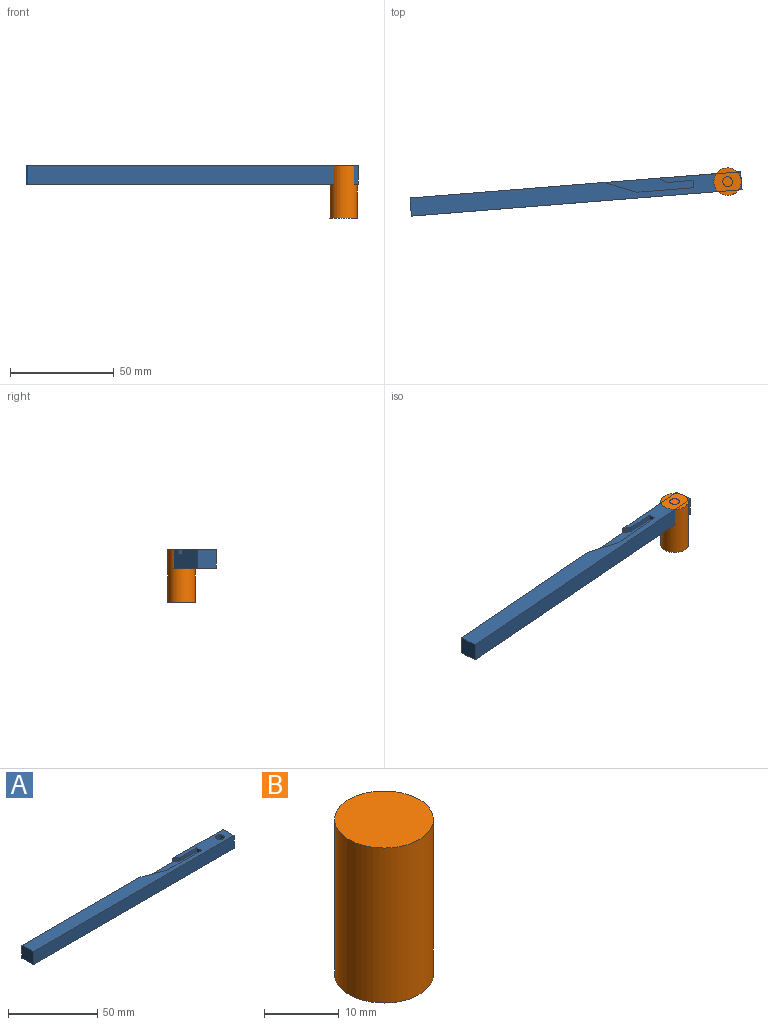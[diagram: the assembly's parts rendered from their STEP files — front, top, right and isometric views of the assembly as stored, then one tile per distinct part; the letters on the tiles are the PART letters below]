
ASSEMBLY  parts=2 mates=1
PART A: 15 faces, bbox 159.6x8.7x8.9 mm
  f0: plane 39.88x0.13mm, normal (0,0,1), area 2.6mm2, adj f3,f4,f9
  f1: plane 42.8x5.93mm, normal (0,0,1), area 172.6mm2, adj f4,f7,f8,f10,f11,f12
  f2: plane 159.63x8.89mm, normal (0,-1,0), area 1419.1mm2, adj f3,f5,f6,f13
  f3: plane 8.89x8.74mm, normal (1,0,0), area 77.4mm2, adj f0,f2,f4,f6,f9,f13
  f4: plane 159.63x8.89mm, normal (0,1,0), area 1251.6mm2, adj f0,f1,f3,f5,f6,f8,f13
  f5: plane 8.89x8.74mm, normal (-1,0,0), area 77.7mm2, adj f2,f4,f6,f13
  f6: plane 159.63x8.74mm, normal (0,0,-1), area 1378.3mm2, adj f2,f3,f4,f5,f14
  f7: plane 27.36x2.54mm, normal (0,1,0), area 69.5mm2, adj f1,f8,f12,f13
  f8: plane 15.45x5.93mm, normal (0.36,0.93,0), area 42mm2, adj f1,f4,f7,f13
  f9: plane 39.88x2.54mm, normal (0,1,0), area 101.3mm2, adj f0,f3,f10,f13
  f10: plane 3.86x2.54mm, normal (-0.53,-0.85,0), area 11.5mm2, adj f1,f9,f11,f13
  f11: plane 12.87x2.54mm, normal (0,-1,0), area 32.7mm2, adj f1,f10,f12,f13
  f12: plane 3.54x2.54mm, normal (-1,0,0), area 9mm2, adj f1,f7,f11,f13
  f13: plane 159.63x8.74mm, normal (0,0,1), area 1203.1mm2, adj f2,f3,f4,f5,f7,f8,f9,f10
  f14: cylinder r=2.34mm len=8.89mm, axis (0,0,1), area 130.9mm2, adj f6,f13
PART B: 3 faces, bbox 13.2x13.2x25.4 mm
  f0: cylinder r=6.62mm len=25.4mm, axis (0,0,-1), area 1056mm2, adj f1,f2
  f1: plane 13.23x13.23mm, normal (0,0,1), area 137.5mm2, adj f0
  f2: plane 13.23x13.23mm, normal (0,0,-1), area 137.5mm2, adj f0
PLACE A rot(axis=(0,0,1),4.6deg) t=(62.85,-4.54,9.46)mm
PLACE B t=(55.93,-0.64,-7.05)mm fixed
MATE revolute B.f0 <-> A.f14  axis (0,0,-1) through (55.93,-0.64,18.35)mm
